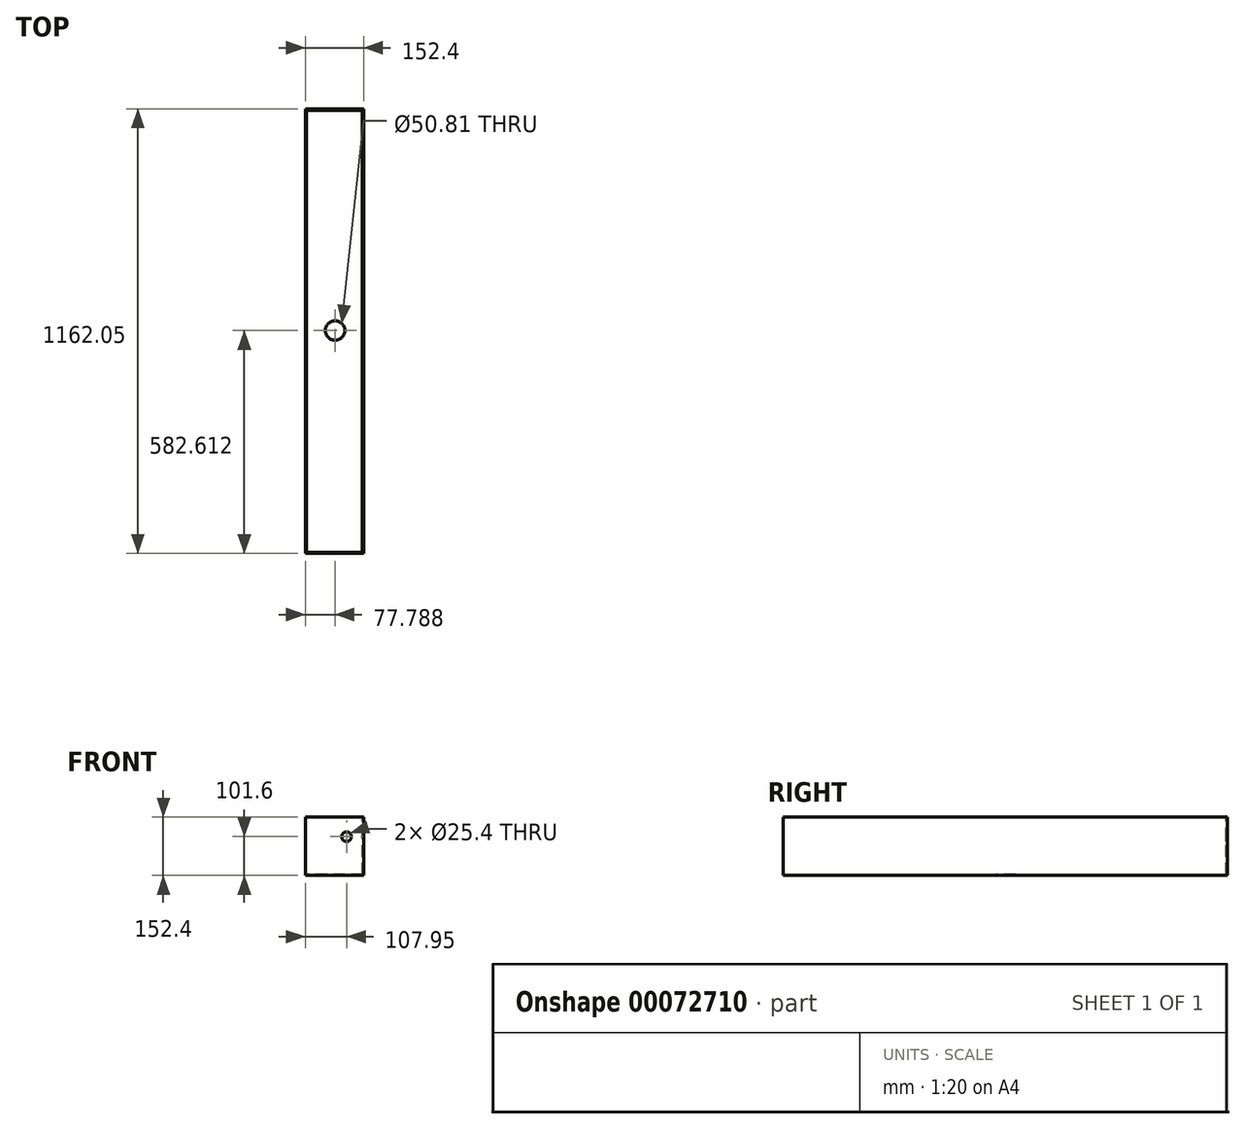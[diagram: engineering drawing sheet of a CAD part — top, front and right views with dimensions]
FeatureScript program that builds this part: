
annotation { "Feature Type Name" : "Feature", "Feature Type Description" : "" }
export const myFeature = defineFeature(function(context is Context, id is Id, definition is map)
    precondition{}
    {
        {
            var Q0;
            Q0=qCreatedBy(makeId("Front.planeOp"),FACE);
            var sketch = newSketch(context, id + "F0", { "sketchPlane" : qUnion([Q0])});
            skLineSegment(sketch, "E0.bottom", {"start": v(0, 0) * mm, "end": v(-152.4, 0) * mm});
            skLineSegment(sketch, "E0.top", {"start": v(0, 152.4) * mm, "end": v(-152.4, 152.4) * mm});
            skLineSegment(sketch, "E0.left", {"start": v(0, 0) * mm, "end": v(0, 152.4) * mm});
            skLineSegment(sketch, "E0.right", {"start": v(-152.4, 0) * mm, "end": v(-152.4, 152.4) * mm});
            skSolve(sketch);
        }
        {
            var Q0;
            Q0=makeQuery(id+"F0.imprint","IMPRINT",FACE,{"disambiguationData":[TD([[makeQuery(id+"F0.imprint","IMPRINT",EDGE,{"derivedFrom":sQuery(id+"F0.wireOp",EDGE,"E0.bottom")}),-1.0]])]});
            extrude(context, id + "F1", {"entities" : qUnion([Q0]), "depth" : 1162.05 * mm});
        }
        {
            var Q0;
            Q0=makeQuery(id+"F1.opExtrude","SWEPT_FACE",FACE,{"disambiguationData":[OSD([sQuery(id+"F0.wireOp",EDGE,"E0.top")])]});
            shell(context, id + "F2", {"entities" : qUnion([Q0]), "thickness" : 3.17 * mm});
        }
        {
            var Q0;
            Q0=makeQuery(id+"F2.opShell","OFFSET_FACE",FACE,{"disambiguationData":[OSD([sQuery(id+"F0.wireOp",EDGE,"E0.bottom")])]});
            var sketch = newSketch(context, id + "F3", { "sketchPlane" : qUnion([Q0])});
            skLineSegment(sketch, "E1.0", {"start": v(-3.17, -1158.88) * mm, "end": v(-3.17, -3.17) * mm});
            skLineSegment(sketch, "E1.1", {"start": v(-3.17, -3.17) * mm, "end": v(-149.22, -3.17) * mm});
            skLineSegment(sketch, "E1.2", {"start": v(-149.22, -1158.88) * mm, "end": v(-149.22, -3.17) * mm});
            skLineSegment(sketch, "E1.3", {"start": v(-3.17, -1158.88) * mm, "end": v(-149.22, -1158.88) * mm});
            skLineSegment(sketch, "E2", {"start": v(0, 0) * mm, "end": v(-149.23, -1158.88) * mm, "construction": true});
            skCircle(sketch, "E3", {"center": v(-74.61, -579.44) * mm, "radius": 25.4 * mm});
            skSolve(sketch);
        }
        {
            var Q0;
            Q0=makeQuery(id+"F3.imprint","IMPRINT",FACE,{"disambiguationData":[TD([[makeQuery(id+"F3.imprint","IMPRINT",EDGE,{"derivedFrom":sQuery(id+"F3.wireOp",EDGE,"E3")}),1.0]])]});
            extrude(context, id + "F4", {"entities" : qUnion([Q0]), "operationType" : NewBodyOperationType.REMOVE, "endBound" : BoundingType.THROUGH_ALL, "oppositeDirection" : true, "depth" : 25.4 * mm});
        }
        {
            var Q0;
            Q0=makeQuery(id+"F1.opExtrude","CAP_FACE",FACE,{"disambiguationData":[OSD([sQuery(id+"F0.wireOp",EDGE,"E0.bottom"),sQuery(id+"F0.wireOp",EDGE,"E0.top"),sQuery(id+"F0.wireOp",EDGE,"E0.left"),sQuery(id+"F0.wireOp",EDGE,"E0.right")])],"isStart":false});
            var sketch = newSketch(context, id + "F5", { "sketchPlane" : qUnion([Q0])});
            skCircle(sketch, "E4", {"center": v(-44.45, 101.6) * mm, "radius": 12.7 * mm});
            skLineSegment(sketch, "E5.0", {"start": v(-152.4, 0) * mm, "end": v(-152.4, 152.4) * mm});
            skLineSegment(sketch, "E5.1", {"start": v(0, 0) * mm, "end": v(0, 152.4) * mm});
            skLineSegment(sketch, "E5.2", {"start": v(0, 152.4) * mm, "end": v(-152.4, 152.4) * mm});
            skLineSegment(sketch, "E5.3", {"start": v(0, 0) * mm, "end": v(-152.4, 0) * mm});
            skSolve(sketch);
        }
        {
            var Q0;
            Q0=makeQuery(id+"F5.imprint","IMPRINT",FACE,{"disambiguationData":[TD([[makeQuery(id+"F5.imprint","IMPRINT",EDGE,{"derivedFrom":sQuery(id+"F5.wireOp",EDGE,"E4")}),1.0]])]});
            extrude(context, id + "F6", {"entities" : qUnion([Q0]), "operationType" : NewBodyOperationType.REMOVE, "endBound" : BoundingType.THROUGH_ALL, "oppositeDirection" : true, "depth" : 25.4 * mm});
        }
    });
